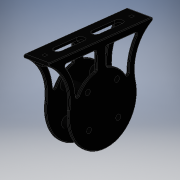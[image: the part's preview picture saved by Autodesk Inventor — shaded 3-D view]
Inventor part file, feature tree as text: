
AUTODESK INVENTOR PART (.ipt)
format: ipt  version: 2016 (Build 200138000, 138)  size: 618,496 bytes
history: native  units: in
note: dims shown in document units (in); Inventor stores cm internally (conversion verified against a paired STEP export)
features: extrude x7, sketch x6, hole x2, plane x2, surface_op x2, projected_geometry x2, fillet x1
ambient origin geometry x8: Origin, YZ Plane, XZ Plane, XY Plane, X Axis, Y Axis, Z Axis, Center Point
bodies: Solid1 (feature_tree)
feature tree (22):
  extrude  "Extrusion1"  Depth=4.225in
  extrude  "Extrusion2"  Depth=0.1in
  sketch  "Sketch3"  dims[d5=0.1in d6=4.0in d7=0.0in]
  hole  "Hole1"  [1 undecoded]
  extrude  "Extrusion4"  Depth=0.1613in
  extrude  "Extrusion5"  Depth=0.025in
  extrude  "Extrusion6"  Depth=0.1in
  extrude  "Extrusion7"  Depth=0.025in
  extrude  "Extrusion8"  Depth=0.025in
  hole  "Hole2"  [1 undecoded]
  fillet  "Fillet1"  Radius=0.125in
  plane  "Work Plane3"
  surface_op  "Replace Face1"
  plane  "Work Plane4"
  surface_op  "Replace Face2"
  sketch  "Sketch1"  dims[d0=1.0in d1=4.225in]
  sketch  "Sketch2"  dims[d2=0.1in d3=0.0in d4=0.1in]
  sketch  "Sketch6"  dims[d8=0.3625in d9=0.1613in]
  sketch  "Sketch8"  dims[d10=0.1in]
  projected_geometry  "Projected Loop1"
  sketch  "Sketch9"  dims[d11=0.15in d12=0.75in d13=0.375in d14=0.25in d15=0.5635in d16=1.0in d17=0.8108in d26=0.3125in d29=0.1in d30=0.15in d31=0.2438in d32=0.125in d33=0.0in d34=0.125in d35=0.0in d36=0.05in d37=0.05in d38=0.2in d39=0.0in d40=0.25in d44=2.5in d45=2.1125in d65=1.125in d69=2.0in d70=2.1125in d71=2.25in d73=0.063in d75=0.063in d76=0.063in d78=0.063in d79=1.5in d80=1.75in d81=0.063in d82=0.125in d83=0.0in d89=1.1811in d90=1.1811in d93=0.375in d95=0.7874in d97=1.1811in d98=0.7874in d100=1.1811in d103=0.125in d104=0.0in d105=0.0984in d106=0.75in d107=0.1969in d108=0.5861in d109=0.5635in d110=1.0in d111=0.8108in d112=0.025in d113=0.0in d114=0.0in]
  projected_geometry  "Projected Loop2"
note: 2 required parameter values undecoded (feature->parameter linkage not recoverable at this tier; creation-order binding heuristic only, values carry confidence <= 0.55)
